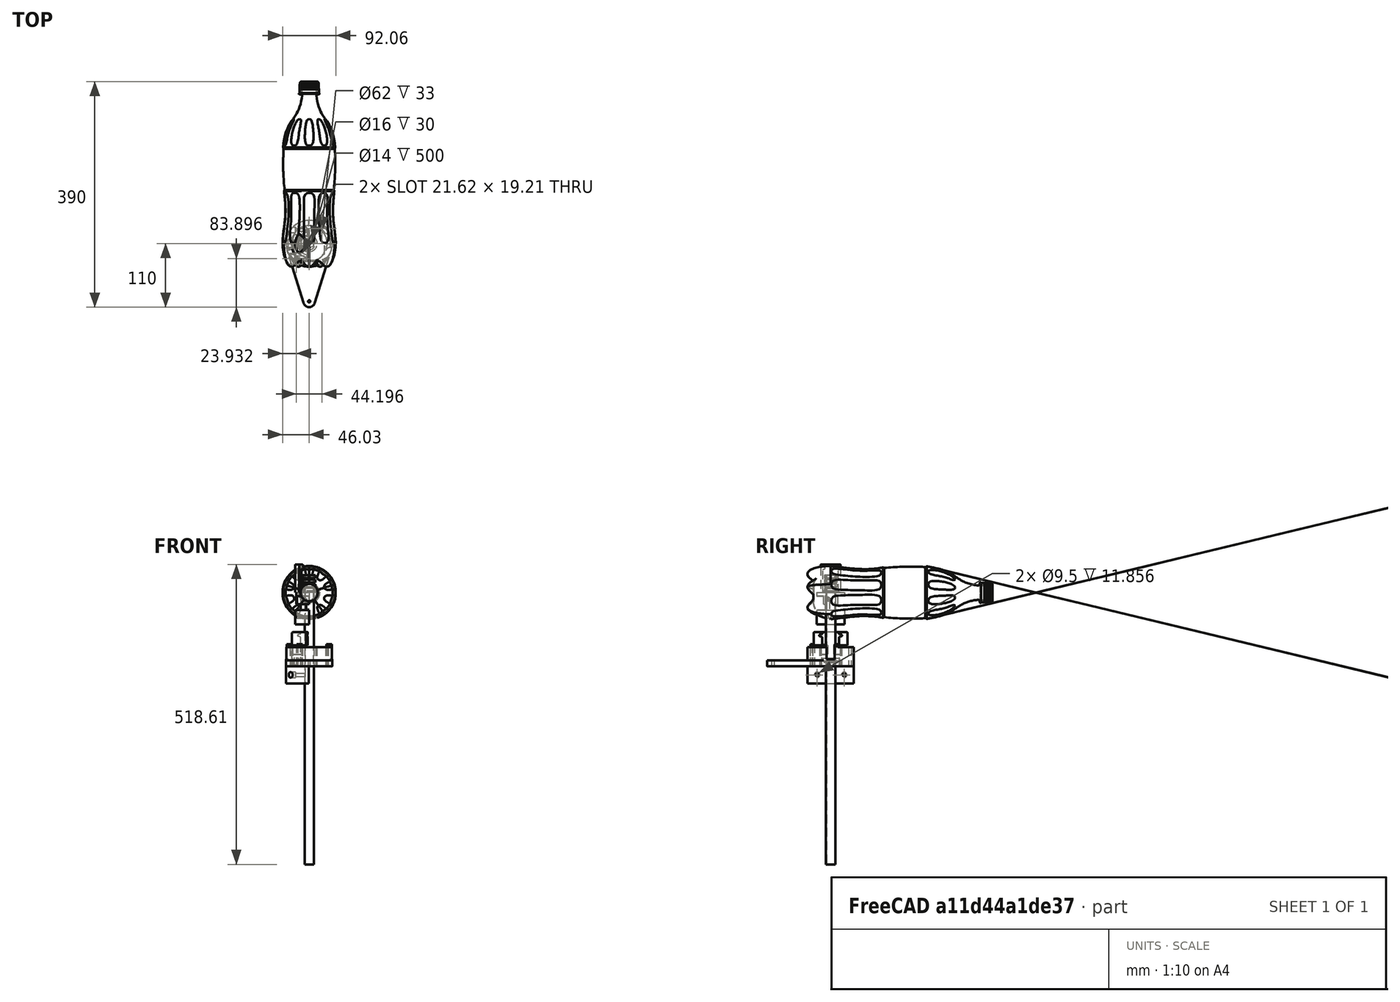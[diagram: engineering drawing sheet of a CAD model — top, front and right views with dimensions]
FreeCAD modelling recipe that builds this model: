
FCSTD DOCUMENT  (FreeCAD 0.17R10694 (Git))
Label: launchBase
License: All rights reserved
LicenseURL: http://en.wikipedia.org/wiki/All_rights_reserved
objects: Sketcher::SketchObject×26, PartDesign::Pocket×13, PartDesign::Plane×12, PartDesign::Pad×10, PartDesign::Body×7, App::Part×5, PartDesign::Line×5, PartDesign::Revolution×3, Mesh::Feature×3, Part::Feature×2, PartDesign::ShapeBinder×2, PartDesign::Fillet×2, PartDesign::AdditiveCylinder×1, PartDesign::SubtractiveCylinder×1, PartDesign::LinearPattern×1, PartDesign::Mirrored×1, PartDesign::Chamfer×1, PartDesign::PolarPattern×1
note: 116 computed .brp shape members not serialized (recipe doc carries the construction recipe); baked Part::Feature solids carry a one-line shape summary decoded from their .brp

FEATURE [Sketcher::SketchObject] Sketch
  MapMode = 5
  Placement = pos=(0,0,0) rot=(1,0,0;1.5708rad)
  Support = -> [XZ_Plane001]
  sketch-geometry (18):
    g0: LineSegment StartX=8 StartY=0 StartZ=0 EndX=8 EndY=30 EndZ=0
    g1: LineSegment StartX=8 StartY=30 StartZ=0 EndX=10.6 EndY=30 EndZ=0
    g2: LineSegment StartX=10.6 StartY=30 StartZ=0 EndX=10.6 EndY=25 EndZ=0
    g3: LineSegment StartX=10.6 StartY=25 StartZ=0 EndX=8.5 EndY=25 EndZ=0
    g4: LineSegment StartX=8.5 StartY=25 StartZ=0 EndX=8.5 EndY=22.5 EndZ=0
    g5: LineSegment StartX=8.5 StartY=22.5 StartZ=0 EndX=10.6 EndY=22.5 EndZ=0
    g6: LineSegment StartX=10.6 StartY=22.5 StartZ=0 EndX=10.6 EndY=17.5 EndZ=0
    g7: LineSegment StartX=10.6 StartY=17.5 StartZ=0 EndX=8.5 EndY=17.5 EndZ=0
    g8: LineSegment StartX=8.5 StartY=17.5 StartZ=0 EndX=8.5 EndY=15 EndZ=0
    g9: LineSegment StartX=8.5 StartY=15 StartZ=0 EndX=10.6 EndY=15 EndZ=0
    g10: LineSegment StartX=10.6 StartY=15 StartZ=0 EndX=10.6 EndY=10 EndZ=0
    g11: LineSegment StartX=10.6 StartY=10 StartZ=0 EndX=8.5 EndY=10 EndZ=0
    g12: LineSegment StartX=8.5 StartY=10 StartZ=0 EndX=8.5 EndY=7.5 EndZ=0
    g13: LineSegment StartX=8.5 StartY=7.5 StartZ=0 EndX=10.6 EndY=7.5 EndZ=0
    g14: LineSegment StartX=14 StartY=0 StartZ=0 EndX=8 EndY=0 EndZ=0
    g15: LineSegment StartX=10.6 StartY=7.5 StartZ=0 EndX=10.6 EndY=3 EndZ=0
    g16: LineSegment StartX=10.6 StartY=3 StartZ=0 EndX=14 EndY=3 EndZ=0
    g17: LineSegment StartX=14 StartY=3 StartZ=0 EndX=14 EndY=0 EndZ=0
  constraints (55):
    c: PointOnObject(g0,g-1)
    c: Vertical(g0)
    c: Coincident(g0,g1)
    c: Horizontal(g1)
    c: Coincident(g1,g2)
    c: Vertical(g2)
    c: Coincident(g2,g3)
    c: Coincident(g3,g4)
    c: Coincident(g4,g5)
    c: Coincident(g5,g6)
    c: Coincident(g6,g7)
    c: Coincident(g7,g8)
    c: Coincident(g8,g9)
    c: Horizontal(g9)
    c: Coincident(g9,g10)
    c: Coincident(g10,g11)
    c: Horizontal(g11)
    c: Coincident(g11,g12)
    c: Coincident(g12,g13)
    c: Coincident(g14,g0)
    c: Horizontal(g14)
    c: DistanceY(g0,g0) = 30
    c: DistanceX(g-1,g0) = 8
    c: Horizontal(g3)
    c: Horizontal(g7)
    c: Horizontal(g13)
    c: DistanceY(g2,g2) = 5
    c: Vertical(g12)
    c: Vertical(g10)
    c: Vertical(g8)
    c: Vertical(g4)
    c: Horizontal(g5)
    c: Equal(g4,g8)
    c: Equal(g8,g12)
    c: DistanceY(g4,g4) = 2.5
    c: Vertical(g6)
    c: Equal(g3,g5)
    c: Equal(g5,g7)
    c: Equal(g7,g9)
    c: Equal(g9,g11)
    c: Equal(g11,g13)
    c: DistanceX(g12) = 8.5
    c: Equal(g6,g10)
    c: DistanceY(g6,g6) = 5
    c: Coincident(g15,g13)
    c: Vertical(g15)
    c: Coincident(g16,g15)
    c: Horizontal(g16)
    c: Coincident(g17,g16)
    c: PointOnObject(g17,g-1)
    c: Vertical(g17)
    c: DistanceX(g1) = 10.6
    c: Coincident(g14,g17)
    c: DistanceX(g14,g14) = 6
    c: DistanceY(g17,g17) = 3
FEATURE [PartDesign::Revolution] Revolution
  Angle = 360
  Axis = (0,0,1)
  Base = (0,0,0)
  Placement = pos=(0,0,0) rot=(1,0,0;1.5708rad)
  Profile = -> Sketch
  ReferenceAxis = -> Sketch [V_Axis]
  Reversed = true
FEATURE [PartDesign::Body] Body
  Group = -> [Sketch,Revolution]
  Origin = -> BodyOrigin
  Tip = -> Revolution
FEATURE [App::Part] Part  label="nozzleHolder"
  Group = -> [Body]
  License = CC BY 3.0
  LicenseURL = http://creativecommons.org/licenses/by/3.0/
  Origin = -> PartOrigin
  Placement = pos=(0,0,-94) rot=(0,0,1;0rad)
FEATURE [PartDesign::AdditiveCylinder] Cylinder
  Angle = 360
  AttacherType = Attacher::AttachEngine3D
  Height = 500
  MapMode = 45
  Placement = pos=(0,0,30) rot=(0,1,0;3.14159rad)
  Radius = 8
  Support = -> [Revolution]
FEATURE [PartDesign::SubtractiveCylinder] Cylinder001
  Angle = 360
  AttacherType = Attacher::AttachEngine3D
  BaseFeature = -> Cylinder
  Height = 1500
  MapMode = 5
  Placement = pos=(0,0,30) rot=(1,0,0;3.14159rad)
  Radius = 7
  Support = -> [Cylinder]
FEATURE [PartDesign::Body] Body001
  Group = -> [Cylinder,Cylinder001]
  Origin = -> Body001Origin
  Tip = -> Cylinder001
FEATURE [App::Part] Part001  label="centralTube"
  Group = -> [Body001]
  License = CC BY 3.0
  LicenseURL = http://creativecommons.org/licenses/by/3.0/
  Origin = -> Part001Origin
  Placement = pos=(0,0,150) rot=(0,0,1;0rad)
FEATURE [Part::Feature] Part__Feature  label="bottle004"
  shape: bbox 37.16 x 19.53 x 37.16 mm, 289 faces (baked)
FEATURE [Part::Feature] Part__Feature001  label="bottle005"
  shape: bbox 103.6 x 317 x 103.7 mm, 79 faces (baked)
FEATURE [App::Part] bottle3  label="bottle006"
  Group = -> [Part__Feature,Part__Feature001]
  License = CC BY 3.0
  LicenseURL = http://creativecommons.org/licenses/by/3.0/
  Origin = -> bottle3Origin
  Placement = pos=(0,0,185) rot=(-1,0,0;1.5708rad)
FEATURE [Sketcher::SketchObject] Sketch001
  MapMode = 5
  Placement = pos=(0,0,0) rot=(1,0,0;1.5708rad)
  Support = -> [XZ_Plane006]
  sketch-geometry (10):
    g0: LineSegment StartX=-13.8661 StartY=42.1125 StartZ=0 EndX=-15.7025 EndY=47.8456 EndZ=0
    g1: LineSegment StartX=-16.75 StartY=48.61 StartZ=0 EndX=-23.14 EndY=48.61 EndZ=0
    g2: LineSegment StartX=-24.16 StartY=47.59 StartZ=0 EndX=-24.16 EndY=0 EndZ=0
    g3: LineSegment StartX=-24.16 StartY=0 StartZ=0 EndX=-19.16 EndY=0 EndZ=0
    g4: LineSegment StartX=-19.16 StartY=0 StartZ=0 EndX=-19.16 EndY=39.34 EndZ=0
    g5: LineSegment StartX=-18.5754 StartY=40.0874 StartZ=0 EndX=-14.4212 EndY=41.1175 EndZ=0
    g6: ArcOfCircle CenterX=-14.6089 CenterY=41.8745 CenterZ=0 NormalX=0 NormalY=0 NormalZ=1 Radius=0.78 StartAngle=4.95545 EndAngle=6.59317
    g7: ArcOfCircle CenterX=-16.75 CenterY=47.51 CenterZ=0 NormalX=0 NormalY=0 NormalZ=1 Radius=1.1 StartAngle=0.309988 EndAngle=1.5708
    g8: ArcOfCircle CenterX=-23.14 CenterY=47.59 CenterZ=0 NormalX=0 NormalY=0 NormalZ=1 Radius=1.02 StartAngle=1.5708 EndAngle=3.14159
    g9: ArcOfCircle CenterX=-18.39 CenterY=39.34 CenterZ=0 NormalX=0 NormalY=0 NormalZ=1 Radius=0.77 StartAngle=1.81386 EndAngle=3.14159
  constraints (26):
    c: Horizontal(g1)
    c: Vertical(g2)
    c: Coincident(g2,g3)
    c: Horizontal(g3)
    c: Coincident(g3,g4)
    c: Vertical(g4)
    c: Tangent(g0,g6) = -1.5708
    c: Tangent(g5,g6) = -1.5708
    c: Tangent(g0,g7) = -1.5708
    c: Tangent(g1,g7) = -1.5708
    c: Tangent(g1,g8) = -1.5708
    c: Tangent(g2,g8) = -1.5708
    c: Tangent(g4,g9) = 1.5708
    c: Tangent(g5,g9) = 1.5708
    c: DistanceX(g3) = -19.16
    c: DistanceY(g3) = 0
    c: DistanceX(g3,g3) = 5
    c: DistanceY(g2,g2) = 47.59
    c: Radius(g8) = 1.02
    c: DistanceX(g1,g1) = 6.39
    c: Radius(g7) = 1.1
    c: Distance(g0) = 6.02
    c: Radius(g6) = 0.78
    c: Distance(g5) = 4.28
    c: Radius(g9) = 0.77
    c: DistanceY(g4,g4) = 39.34
FEATURE [PartDesign::Revolution] Revolution001
  Angle = 90
  Axis = (0,0,1)
  Base = (0,0,0)
  Midplane = true
  Placement = pos=(0,0,0) rot=(1,0,0;1.5708rad)
  Profile = -> Sketch001
  ReferenceAxis = -> Sketch001 [V_Axis]
FEATURE [Sketcher::SketchObject] Sketch002
  ExternalGeometry = -> [Revolution001]
  MapMode = 5
  Placement = pos=(0,0,0) rot=(1,0,0;3.14159rad)
  Support = -> [Revolution001]
  sketch-geometry (4):
    g0: ArcOfCircle CenterX=0 CenterY=0 CenterZ=0 NormalX=0 NormalY=0 NormalZ=1 Radius=24.16 StartAngle=1.5708 EndAngle=4.71239
    g1: ArcOfCircle CenterX=0 CenterY=0 CenterZ=0 NormalX=0 NormalY=0 NormalZ=1 Radius=9 StartAngle=1.5708 EndAngle=4.71239
    g2: LineSegment StartX=0 StartY=24.16 StartZ=0 EndX=0 EndY=9 EndZ=0
    g3: LineSegment StartX=0 StartY=-9 StartZ=0 EndX=0 EndY=-24.16 EndZ=0
  constraints (13):
    c: Coincident(g0,g-1)
    c: Coincident(g0,g-3)
    c: Coincident(g0,g-3)
    c: Coincident(g1,g-1)
    c: PointOnObject(g1,g-2)
    c: PointOnObject(g1,g-2)
    c: Coincident(g2,g0)
    c: Vertical(g2)
    c: Coincident(g3,g1)
    c: Vertical(g3)
    c: Radius(g1) = 9
    c: Coincident(g0,g3)
    c: Coincident(g2,g1)
FEATURE [PartDesign::Pad] Pad
  BaseFeature = -> Revolution001
  Length = 20
  Length2 = 100
  Placement = pos=(0,0,0) rot=(1,0,0;1.5708rad)
  Profile = -> Sketch002
  Type = 0
FEATURE [Sketcher::SketchObject] Sketch003
  ExternalGeometry = -> [Pad]
  MapMode = 5
  Placement = pos=(0,0,0) rot=(0.707107,0,0.707107;3.14159rad)
  Support = -> [Pad]
  sketch-geometry (8):
    g0: LineSegment StartX=-20 StartY=24.16 StartZ=0 EndX=-6 EndY=24.16 EndZ=0
    g1: LineSegment StartX=-6 StartY=24.16 StartZ=0 EndX=-6 EndY=12 EndZ=0
    g2: LineSegment StartX=-6 StartY=12 StartZ=0 EndX=-20 EndY=12 EndZ=0
    g3: LineSegment StartX=-20 StartY=12 StartZ=0 EndX=-20 EndY=24.16 EndZ=0
    g4: LineSegment StartX=-20 StartY=-24.16 StartZ=0 EndX=-6 EndY=-24.16 EndZ=0
    g5: LineSegment StartX=-6 StartY=-24.16 StartZ=0 EndX=-6 EndY=-12 EndZ=0
    g6: LineSegment StartX=-6 StartY=-12 StartZ=0 EndX=-20 EndY=-12 EndZ=0
    g7: LineSegment StartX=-20 StartY=-12 StartZ=0 EndX=-20 EndY=-24.16 EndZ=0
  constraints (18):
    c: Coincident(g0,g1)
    c: Coincident(g1,g2)
    c: Coincident(g2,g3)
    c: Coincident(g3,g0)
    c: Horizontal(g0)
    c: Horizontal(g2)
    c: Vertical(g1)
    c: Vertical(g3)
    c: Coincident(g4,g5)
    c: Coincident(g5,g6)
    c: Coincident(g6,g7)
    c: Coincident(g7,g4)
    c: Horizontal(g4)
    c: Horizontal(g6)
    c: Vertical(g5)
    c: Vertical(g7)
    c: Equal(g6,g2)
    c: Equal(g1,g5)
FEATURE [PartDesign::Pocket] Pocket
  BaseFeature = -> Pad
  Length = 5
  Placement = pos=(0,0,0) rot=(1,0,0;1.5708rad)
  Profile = -> Sketch003
  Type = 1
FEATURE [Sketcher::SketchObject] Sketch004
  ExternalGeometry = -> [Pocket]
  MapMode = 5
  Placement = pos=(0,0,-6) rot=(1,0,0;3.14159rad)
  Support = -> [Pocket]
  sketch-geometry (1):
    g0: Circle CenterX=-10 CenterY=-5 CenterZ=0 NormalX=0 NormalY=0 NormalZ=1 Radius=2
  constraints (3):
    c: Radius(g0) = 2
    c: DistanceY(g-3,g0) = 7
    c: DistanceX(g0,g-3) = 10
FEATURE [PartDesign::Pocket] Pocket001
  BaseFeature = -> Pocket
  Length = 5
  Placement = pos=(0,0,0) rot=(1,0,0;1.5708rad)
  Profile = -> Sketch004
  Type = 1
FEATURE [PartDesign::Line] DatumLine
  AttacherType = Attacher::AttachEngineLine
  MapMode = 19
  Placement = pos=(-10,0,-13) rot=(1,0,0;1.5708rad)
FEATURE [Sketcher::SketchObject] Sketch007
  ExternalGeometry = -> [Pocket001]
  MapMode = 5
  Placement = pos=(0,0,-20) rot=(1,0,0;3.14159rad)
  Support = -> [Pocket001]
  sketch-geometry (4):
    g0: LineSegment StartX=-25 StartY=-9 StartZ=0 EndX=0 EndY=-9 EndZ=0
    g1: LineSegment StartX=0 StartY=-9 StartZ=0 EndX=0 EndY=9 EndZ=0
    g2: LineSegment StartX=0 StartY=9 StartZ=0 EndX=-25 EndY=9 EndZ=0
    g3: LineSegment StartX=-25 StartY=9 StartZ=0 EndX=-25 EndY=-9 EndZ=0
  constraints (11):
    c: Coincident(g0,g1)
    c: Coincident(g1,g2)
    c: Coincident(g2,g3)
    c: Coincident(g3,g0)
    c: Horizontal(g0)
    c: Horizontal(g2)
    c: Vertical(g1)
    c: Vertical(g3)
    c: Symmetric(g0,g1,g-1)
    c: Coincident(g0,g-3)
    c: DistanceX(g0,g0) = 25
FEATURE [PartDesign::Pocket] Pocket002
  BaseFeature = -> Pocket001
  Length = 20
  Placement = pos=(0,0,0) rot=(1,0,0;1.5708rad)
  Profile = -> Sketch007
  Type = 0
FEATURE [PartDesign::Body] Body002  label="clamp"
  Group = -> [Sketch001,Revolution001,Sketch002,Pad,Sketch003,Pocket,Sketch004,Pocket001,Sketch007,Pocket002]
  Origin = -> Body002Origin
  Tip = -> Pocket002
FEATURE [PartDesign::ShapeBinder] ReferencePocket002
  Placement = pos=(0,0,0) rot=(1,0,0;1.5708rad)
  Support = -> [Pocket002]
FEATURE [PartDesign::Plane] DatumPlane
  MapMode = 5
  Placement = pos=(0,-9,0) rot=(-1,0,0;1.5708rad)
  Support = -> [ReferencePocket002]
FEATURE [Sketcher::SketchObject] Sketch008
  ExternalGeometry = -> [ReferencePocket002]
  MapMode = 5
  Placement = pos=(0,-9,0) rot=(-1,0,0;1.5708rad)
  Support = -> [DatumPlane]
  sketch-geometry (6):
    g0: Circle CenterX=-10 CenterY=13 CenterZ=0 NormalX=0 NormalY=0 NormalZ=1 Radius=2
    g1: ArcOfCircle CenterX=-10 CenterY=13 CenterZ=0 NormalX=0 NormalY=0 NormalZ=1 Radius=5 StartAngle=3.14159 EndAngle=6.28319
    g2: LineSegment [constr] StartX=-15 StartY=13 StartZ=0 EndX=-5 EndY=13 EndZ=0
    g3: LineSegment StartX=-15 StartY=13 StartZ=0 EndX=-15 EndY=30 EndZ=0
    g4: LineSegment StartX=-15 StartY=30 StartZ=0 EndX=-5 EndY=30 EndZ=0
    g5: LineSegment StartX=-5 StartY=30 StartZ=0 EndX=-5 EndY=13 EndZ=0
  constraints (16):
    c: Coincident(g0,g-3)
    c: Equal(g0,g-3)
    c: Coincident(g1,g0)
    c: Coincident(g2,g1)
    c: Horizontal(g2)
    c: PointOnObject(g0,g2)
    c: Coincident(g1,g2)
    c: Vertical(g3)
    c: Coincident(g3,g4)
    c: Horizontal(g4)
    c: Coincident(g4,g5)
    c: Coincident(g5,g1)
    c: Vertical(g5)
    c: DistanceX(g4,g4) = 10
    c: DistanceY(g5,g5) = 17
    c: Coincident(g1,g3)
FEATURE [PartDesign::Pad] Pad001
  Length = 11
  Length2 = 100
  Placement = pos=(0,-9,0) rot=(-1,0,0;1.5708rad)
  Profile = -> Sketch008
  Type = 0
FEATURE [PartDesign::Plane] DatumPlane001
  MapMode = 5
  Placement = pos=(0,-9,-30) rot=(0,1,0;3.14159rad)
  Support = -> [Pad001]
FEATURE [PartDesign::ShapeBinder] ReferenceRevolution
  Placement = pos=(0,0,0) rot=(1,0,0;1.5708rad)
  Support = -> [Revolution]
FEATURE [PartDesign::Line] DatumLine001
  AttacherType = Attacher::AttachEngineLine
  MapMode = 42
  Support = -> [ReferenceRevolution]
FEATURE [Sketcher::SketchObject] Sketch009
  ExternalGeometry = -> [DatumLine001]
  MapMode = 5
  Placement = pos=(0,-9,-30) rot=(0,1,0;3.14159rad)
  Support = -> [DatumPlane001]
  sketch-geometry (4):
    g0: ArcOfCircle CenterX=0 CenterY=9 CenterZ=0 NormalX=0 NormalY=0 NormalZ=1 Radius=24 StartAngle=4.71239 EndAngle=7.85398
    g1: LineSegment StartX=0 StartY=33 StartZ=0 EndX=0 EndY=17 EndZ=0
    g2: ArcOfCircle CenterX=0 CenterY=9 CenterZ=0 NormalX=0 NormalY=0 NormalZ=1 Radius=8 StartAngle=4.71239 EndAngle=7.85398
    g3: LineSegment StartX=0 StartY=1 StartZ=0 EndX=0 EndY=-15 EndZ=0
  constraints (13):
    c: Coincident(g0,g-3)
    c: PointOnObject(g0,g-2)
    c: PointOnObject(g1,g-2)
    c: Vertical(g1)
    c: Coincident(g2,g0)
    c: Coincident(g2,g1)
    c: PointOnObject(g2,g-2)
    c: Coincident(g3,g2)
    c: Coincident(g3,g0)
    c: Vertical(g3)
    c: Radius(g2) = 8
    c: Radius(g0) = 24
    c: Coincident(g1,g0)
FEATURE [PartDesign::Pad] Pad002
  BaseFeature = -> Pad001
  Length = 25
  Length2 = 100
  Placement = pos=(0,-9,0) rot=(-1,0,0;1.5708rad)
  Profile = -> Sketch009
  Type = 0
FEATURE [PartDesign::LinearPattern] LinearPattern
  BaseFeature = -> Pad002
  Direction = -> Sketch008 [N_Axis]
  Length = 35
  Occurrences = 2
  Originals = -> [Pad001]
  Placement = pos=(0,-9,0) rot=(-1,0,0;1.5708rad)
  Reversed = true
FEATURE [Sketcher::SketchObject] Sketch010
  ExternalGeometry = -> [LinearPattern]
  MapMode = 5
  Placement = pos=(0,-9,0) rot=(0,1,0;1.5708rad)
  Support = -> [LinearPattern]
  sketch-geometry (4):
    g0: LineSegment [constr] StartX=30 StartY=12 StartZ=0 EndX=55 EndY=-4 EndZ=0
    g1: LineSegment [constr] StartX=30 StartY=-36 StartZ=0 EndX=55 EndY=-20 EndZ=0
    g2: Circle CenterX=42.5 CenterY=4 CenterZ=0 NormalX=0 NormalY=0 NormalZ=1 Radius=2
    g3: Circle CenterX=42.5 CenterY=-28 CenterZ=0 NormalX=0 NormalY=0 NormalZ=1 Radius=2
  constraints (6):
    c: PointOnObject(g2,g0)
    c: PointOnObject(g3,g1)
    c: Equal(g2,g3)
    c: Symmetric(g0,g0,g2)
    c: Symmetric(g1,g1,g3)
    c: Radius(g3) = 2
FEATURE [PartDesign::Pocket] Pocket003
  BaseFeature = -> LinearPattern
  Length = 5
  Placement = pos=(0,-9,0) rot=(-1,0,0;1.5708rad)
  Profile = -> Sketch010
  Type = 1
FEATURE [Sketcher::SketchObject] Sketch012
  ExternalGeometry = -> [Pocket003]
  MapMode = 5
  Placement = pos=(0,-9,-30) rot=(0,1,0;3.14159rad)
  Support = -> [DatumPlane001]
  sketch-geometry (4):
    g0: ArcOfCircle CenterX=0 CenterY=-12 CenterZ=0 NormalX=0 NormalY=0 NormalZ=1 Radius=31.88 StartAngle=4.71239 EndAngle=7.85398
    g1: ArcOfCircle CenterX=0 CenterY=-12 CenterZ=0 NormalX=0 NormalY=0 NormalZ=1 Radius=20 StartAngle=4.71239 EndAngle=7.85398
    g2: LineSegment StartX=0 StartY=19.88 StartZ=0 EndX=0 EndY=8 EndZ=0
    g3: LineSegment StartX=0 StartY=-32 StartZ=0 EndX=0 EndY=-43.88 EndZ=0
  constraints (15):
    c: PointOnObject(g0,g-2)
    c: PointOnObject(g0,g-2)
    c: PointOnObject(g1,g-2)
    c: PointOnObject(g1,g-2)
    c: PointOnObject(g1,g-2)
    c: Coincident(g0,g1)
    c: Coincident(g0,g-3)
    c: Radius(g1) = 20
    c: PointOnObject(g2,g-2)
    c: PointOnObject(g2,g-2)
    c: Coincident(g1,g2)
    c: Coincident(g0,g2)
    c: Coincident(g0,g3)
    c: Coincident(g1,g3)
    c: Radius(g0) = 31.88
FEATURE [PartDesign::Pocket] Pocket005
  BaseFeature = -> Pocket003
  Length = 25
  Placement = pos=(0,-9,0) rot=(-1,0,0;1.5708rad)
  Profile = -> Sketch012
  Type = 0
FEATURE [PartDesign::Body] Body003  label="fixation"
  Group = -> [DatumLine,DatumPlane,ReferencePocket002,Sketch008,Pad001,DatumPlane001,DatumLine001,ReferenceRevolution,Sketch009,Pad002,LinearPattern,Sketch010,Pocket003,Sketch012,Pocket005]
  Origin = -> Body003Origin
  Tip = -> Pocket005
FEATURE [App::Part] Part002  label="releasmechanism"
  Group = -> [Body002,Body003]
  License = CC BY 3.0
  LicenseURL = http://creativecommons.org/licenses/by/3.0/
  Origin = -> Part002Origin
  Placement = pos=(0,0,-113) rot=(0,0,1;0rad)
FEATURE [Sketcher::SketchObject] Sketch013
  MapMode = 5
  Placement = pos=(0,0,0) rot=(1,0,0;1.5708rad)
  Support = -> [XZ_Plane009]
  sketch-geometry (14):
    g0: LineSegment StartX=-14.5926 StartY=-91.2916 StartZ=0 EndX=-14.5926 EndY=-78.1016 EndZ=0
    g1: LineSegment StartX=-15.6271 StartY=-76.6684 StartZ=0 EndX=-19.0629 EndY=-75.5285 EndZ=0
    g2: LineSegment StartX=-19.8645 StartY=-74.4181 StartZ=0 EndX=-19.8645 EndY=-73.7281 EndZ=0
    g3: LineSegment StartX=-19.1362 StartY=-72.7285 StartZ=0 EndX=-15.1 EndY=-71.4297 EndZ=0
    g4: LineSegment StartX=-14.4411 StartY=-70.3425 StartZ=0 EndX=-14.6117 EndY=-69.347 EndZ=0
    g5: LineSegment StartX=-15.9226 StartY=-68.2416 StartZ=0 EndX=-27.9326 EndY=-68.2416 EndZ=0
    g6: LineSegment StartX=-29.6526 StartY=-69.9616 StartZ=0 EndX=-29.6526 EndY=-91.2916 EndZ=0
    g7: LineSegment StartX=-29.6526 StartY=-91.2916 StartZ=0 EndX=-14.5926 EndY=-91.2916 EndZ=0
    g8: ArcOfCircle CenterX=-16.1026 CenterY=-78.1016 CenterZ=0 NormalX=0 NormalY=0 NormalZ=1 Radius=1.51 StartAngle=0 EndAngle=1.25046
    g9: ArcOfCircle CenterX=-18.6945 CenterY=-74.4181 CenterZ=0 NormalX=0 NormalY=0 NormalZ=1 Radius=1.17 StartAngle=3.14159 EndAngle=4.39205
    g10: ArcOfCircle CenterX=-18.8145 CenterY=-73.7281 CenterZ=0 NormalX=0 NormalY=0 NormalZ=1 Radius=1.05 StartAngle=1.88214 EndAngle=3.14159
    g11: ArcOfCircle CenterX=-15.3972 CenterY=-70.5063 CenterZ=0 NormalX=0 NormalY=0 NormalZ=1 Radius=0.97 StartAngle=5.02373 EndAngle=6.4529
    g12: ArcOfCircle CenterX=-15.9226 CenterY=-69.5716 CenterZ=0 NormalX=0 NormalY=0 NormalZ=1 Radius=1.33 StartAngle=0.16971 EndAngle=1.5708
    g13: ArcOfCircle CenterX=-27.9326 CenterY=-69.9616 CenterZ=0 NormalX=0 NormalY=0 NormalZ=1 Radius=1.72 StartAngle=1.5708 EndAngle=3.14159
  constraints (36):
    c: Vertical(g2)
    c: Horizontal(g5)
    c: Vertical(g6)
    c: Coincident(g6,g7)
    c: Coincident(g7,g0)
    c: Horizontal(g7)
    c: Vertical(g0)
    c: Tangent(g0,g8) = -1.5708
    c: Tangent(g1,g8) = -1.5708
    c: Tangent(g1,g9) = 1.5708
    c: Tangent(g2,g9) = 1.5708
    c: Tangent(g2,g10) = 1.5708
    c: Tangent(g3,g10) = 1.5708
    c: Tangent(g3,g11) = -1.5708
    c: Tangent(g4,g11) = -1.5708
    c: Tangent(g4,g12) = -1.5708
    c: Tangent(g5,g12) = -1.5708
    c: Tangent(g5,g13) = -1.5708
    c: Tangent(g6,g13) = -1.5708
    c: DistanceY(g6,g6) = 21.33
    c: Radius(g13) = 1.72
    c: DistanceX(g5,g5) = 12.01
    c: Radius(g12) = 1.33
    c: Distance(g4) = 1.01
    c: Radius(g11) = 0.97
    c: Distance(g3) = 4.24
    c: Radius(g10) = 1.05
    c: DistanceY(g2,g2) = 0.69
    c: Radius(g9) = 1.17
    c: Distance(g1) = 3.62
    c: Radius(g8) = 1.51
    c: DistanceY(g0,g0) = 13.19
    c: DistanceX(g7,g7) = 15.06
    c: DistanceX(g0) = -14.5926
    c: DistanceY(g0) = -91.2916
    c: DistanceY(g1,g3) = 2.8
FEATURE [PartDesign::Revolution] Revolution002
  Angle = 160
  Axis = (0,0,1)
  Base = (0,0,0)
  Midplane = true
  Placement = pos=(0,0,0) rot=(1,0,0;1.5708rad)
  Profile = -> Sketch013
  ReferenceAxis = -> Sketch013 [V_Axis]
FEATURE [Sketcher::SketchObject] Sketch014
  ExternalGeometry = -> [Revolution002]
  MapMode = 5
  Placement = pos=(0,0,-91.2916) rot=(1,0,0;3.14159rad)
  Support = -> [Revolution002]
  sketch-geometry (4):
    g0: LineSegment StartX=-29.228 StartY=5 StartZ=0 EndX=-13.7092 EndY=5 EndZ=0
    g1: LineSegment StartX=-29.228 StartY=-5 StartZ=0 EndX=-13.7092 EndY=-5 EndZ=0
    g2: ArcOfCircle CenterX=0 CenterY=0 CenterZ=0 NormalX=0 NormalY=0 NormalZ=1 Radius=29.6526 StartAngle=2.97216 EndAngle=3.31102
    g3: ArcOfCircle CenterX=0 CenterY=0 CenterZ=0 NormalX=0 NormalY=0 NormalZ=1 Radius=14.5926 StartAngle=2.79187 EndAngle=3.49132
  constraints (14):
    c: PointOnObject(g0,g-3)
    c: PointOnObject(g0,g-4)
    c: Horizontal(g0)
    c: PointOnObject(g1,g-3)
    c: PointOnObject(g1,g-4)
    c: Horizontal(g1)
    c: Coincident(g2,g-1)
    c: Coincident(g2,g0)
    c: Coincident(g2,g1)
    c: Coincident(g3,g-1)
    c: Coincident(g3,g0)
    c: Coincident(g3,g1)
    c: Symmetric(g0,g1,g-1)
    c: DistanceY(g1,g0) = 10
FEATURE [PartDesign::Pad] Pad003
  BaseFeature = -> Revolution002
  Length = 35
  Length2 = 100
  Placement = pos=(0,0,0) rot=(1,0,0;1.5708rad)
  Profile = -> Sketch014
  Type = 0
FEATURE [PartDesign::Fillet] Fillet
  Base = -> Pad003 [Edge50]
  BaseFeature = -> Pad003
  Placement = pos=(0,0,0) rot=(1,0,0;1.5708rad)
  Radius = 10
FEATURE [Sketcher::SketchObject] Sketch016
  ExternalGeometry = -> [Fillet]
  MapMode = 5
  Placement = pos=(0,-5,0) rot=(1,0,0;1.5708rad)
  Support = -> [Fillet]
  sketch-geometry (3):
    g0: LineSegment [constr] StartX=-19.0059 StartY=-126.292 StartZ=0 EndX=-19.0059 EndY=-116.292 EndZ=0
    g1: LineSegment [constr] StartX=-29.228 StartY=-116.292 StartZ=0 EndX=-19.0059 EndY=-116.292 EndZ=0
    g2: Circle CenterX=-19.0059 CenterY=-116.292 CenterZ=0 NormalX=0 NormalY=0 NormalZ=1 Radius=2.1
  constraints (7):
    c: Vertical(g0)
    c: Coincident(g1,g0)
    c: Horizontal(g1)
    c: Coincident(g2,g0)
    c: Radius(g2) = 2.1
    c: Coincident(g0,g-3)
    c: Coincident(g1,g-4)
FEATURE [PartDesign::Pocket] Pocket006
  BaseFeature = -> Fillet
  Length = 5
  Placement = pos=(0,0,0) rot=(1,0,0;1.5708rad)
  Profile = -> Sketch016
  Type = 1
FEATURE [PartDesign::Body] Body004  label="Clamp"
  Group = -> [Sketch013,Revolution002,Sketch014,Pad003,Fillet,Sketch016,Pocket006]
  Origin = -> Body004Origin
  Tip = -> Pocket006
FEATURE [PartDesign::Plane] DatumPlane002
  MapMode = 5
  Placement = pos=(0,0,-127.292) rot=(1,0,0;3.14159rad)
  Support = -> [Pocket006]
  superPlacement = pos=(0,0,1) rot=(0,0,1;0rad)
FEATURE [Sketcher::SketchObject] Sketch017
  MapMode = 5
  Placement = pos=(0,0,-127.292) rot=(1,0,0;3.14159rad)
  Support = -> [DatumPlane002]
  sketch-geometry (4):
    g0: ArcOfCircle CenterX=0 CenterY=0 CenterZ=0 NormalX=0 NormalY=0 NormalZ=1 Radius=7 StartAngle=1.71414 EndAngle=4.56904
    g1: LineSegment StartX=-1 StartY=6.9282 StartZ=0 EndX=-1 EndY=39.9875 EndZ=0
    g2: ArcOfCircle CenterX=0 CenterY=0 CenterZ=0 NormalX=0 NormalY=0 NormalZ=1 Radius=40 StartAngle=1.5958 EndAngle=4.68739
    g3: LineSegment StartX=-1 StartY=-6.9282 StartZ=0 EndX=-1 EndY=-39.9875 EndZ=0
  constraints (12):
    c: Coincident(g0,g-1)
    c: DistanceX(g0,g-1) = 1
    c: Coincident(g1,g0)
    c: Vertical(g1)
    c: Coincident(g2,g-1)
    c: Coincident(g2,g1)
    c: Coincident(g3,g0)
    c: Coincident(g3,g2)
    c: Vertical(g3)
    c: Symmetric(g0,g0,g-1)
    c: Radius(g0) = 7
    c: Radius(g2) = 40
FEATURE [PartDesign::Pad] Pad004
  Length = 30
  Length2 = 100
  Placement = pos=(0,0,-127.292) rot=(1,0,0;3.14159rad)
  Profile = -> Sketch017
  Type = 0
FEATURE [PartDesign::Plane] DatumPlane003
  MapMode = 5
  Placement = pos=(0,-5,0) rot=(1,0,0;1.5708rad)
  Support = -> [Pocket006]
FEATURE [PartDesign::Plane] DatumPlane004
  MapMode = 5
  Placement = pos=(0,5,0) rot=(-1,0,0;1.5708rad)
  Support = -> [Pocket006]
FEATURE [PartDesign::Plane] DatumPlane005
  MapMode = 45
  Placement = pos=(-29.5109,0,-103.792) rot=(0.57735,0.57735,0.57735;2.0944rad)
  Support = -> [Pocket006]
FEATURE [Sketcher::SketchObject] Sketch018
  ExternalGeometry = -> [DatumPlane005,DatumPlane004,DatumPlane003,Pad004]
  MapMode = 5
  Placement = pos=(0,0,-127.292) rot=(0,0,1;0rad)
  Support = -> [Pad004]
  sketch-geometry (4):
    g0: ArcOfCircle CenterX=0 CenterY=0 CenterZ=0 NormalX=0 NormalY=0 NormalZ=1 Radius=30.0191 StartAngle=3.32585 EndAngle=3.68416
    g1: LineSegment StartX=-25.7079 StartY=-15.5 StartZ=0 EndX=-13.7079 EndY=-15.5 EndZ=0
    g2: LineSegment StartX=-13.7079 StartY=-15.5 StartZ=0 EndX=-13.7079 EndY=-5.5 EndZ=0
    g3: LineSegment StartX=-13.7079 StartY=-5.5 StartZ=0 EndX=-29.5109 EndY=-5.5 EndZ=0
  constraints (12):
    c: Coincident(g0,g-1)
    c: Coincident(g1,g0)
    c: Horizontal(g1)
    c: Vertical(g2)
    c: Coincident(g3,g2)
    c: Coincident(g3,g0)
    c: Horizontal(g3)
    c: Coincident(g1,g2)
    c: DistanceY(g2,g2) = 10
    c: PointOnObject(g0,g-3)
    c: DistanceY(g2,g-1) = 5.5
    c: DistanceX(g1,g1) = 12
FEATURE [PartDesign::Pad] Pad005
  BaseFeature = -> Pad004
  Length = 20
  Length2 = 100
  Placement = pos=(0,0,-127.292) rot=(1,0,0;3.14159rad)
  Profile = -> Sketch018
  Type = 0
FEATURE [PartDesign::Mirrored] Mirrored
  BaseFeature = -> Pad005
  MirrorPlane = -> Sketch018 [H_Axis]
  Originals = -> [Pad005]
  Placement = pos=(0,0,-127.292) rot=(1,0,0;3.14159rad)
FEATURE [PartDesign::Line] DatumLine002
  AttacherType = Attacher::AttachEngineLine
  MapMode = 19
  Placement = pos=(-19.0059,-5,-116.292) rot=(1,0,0;1.5708rad)
  Support = -> [Pocket006]
FEATURE [Sketcher::SketchObject] Sketch019
  ExternalGeometry = -> [DatumLine002]
  MapMode = 5
  Placement = pos=(0,-15.5,-127.292) rot=(0,0.707107,-0.707107;3.14159rad)
  Support = -> [Mirrored]
  sketch-geometry (1):
    g0: Circle CenterX=19.0059 CenterY=-11 CenterZ=0 NormalX=0 NormalY=0 NormalZ=1 Radius=2.1
  constraints (2):
    c: Coincident(g0,g-3)
    c: Radius(g0) = 2.1
FEATURE [PartDesign::Pocket] Pocket007
  BaseFeature = -> Mirrored
  Length = 5
  Placement = pos=(0,0,-127.292) rot=(1,0,0;3.14159rad)
  Profile = -> Sketch019
  Type = 1
FEATURE [Sketcher::SketchObject] Sketch020
  ExternalGeometry = -> [Pocket007]
  MapMode = 5
  Placement = pos=(-1,0,-127.292) rot=(0.57735,-0.57735,0.57735;4.18879rad)
  Support = -> [Pocket007]
  sketch-geometry (4):
    g0: LineSegment [constr] StartX=-39.9875 StartY=0 StartZ=0 EndX=-6.9282 EndY=30 EndZ=0
    g1: LineSegment [constr] StartX=6.9282 StartY=30 StartZ=0 EndX=39.9875 EndY=0 EndZ=0
    g2: Circle CenterX=-23.4579 CenterY=15 CenterZ=0 NormalX=0 NormalY=0 NormalZ=1 Radius=2.6
    g3: Circle CenterX=23.4579 CenterY=15 CenterZ=0 NormalX=0 NormalY=0 NormalZ=1 Radius=2.6
  constraints (11):
    c: Coincident(g0,g-4)
    c: Coincident(g0,g-3)
    c: Coincident(g1,g-5)
    c: PointOnObject(g1,g-1)
    c: Coincident(g1,g-6)
    c: PointOnObject(g2,g0)
    c: PointOnObject(g3,g1)
    c: Radius(g3) = 2.6
    c: Equal(g3,g2)
    c: Symmetric(g0,g0,g2)
    c: Symmetric(g1,g1,g3)
FEATURE [PartDesign::Pocket] Pocket008
  BaseFeature = -> Pocket007
  Length = 5
  Placement = pos=(0,0,-127.292) rot=(1,0,0;3.14159rad)
  Profile = -> Sketch020
  Type = 1
FEATURE [PartDesign::Plane] DatumPlane006
  MapMode = 45
  Placement = pos=(-33,-23.4579,-142.292) rot=(0.707107,0,0.707107;3.14159rad)
  Support = -> [Pocket008]
  superPlacement = pos=(0,0,-32) rot=(0,0,1;0rad)
FEATURE [PartDesign::Line] DatumLine003
  AttacherType = Attacher::AttachEngineLine
  MapMode = 19
  Placement = pos=(-1,23.4579,-142.292) rot=(0.57735,-0.57735,0.57735;4.18879rad)
  Support = -> [Pocket008]
FEATURE [PartDesign::Line] DatumLine004
  AttacherType = Attacher::AttachEngineLine
  MapMode = 19
  Placement = pos=(-1,-23.4579,-142.292) rot=(0.57735,-0.57735,0.57735;4.18879rad)
  Support = -> [Pocket008]
FEATURE [Sketcher::SketchObject] Sketch021
  ExternalGeometry = -> [DatumLine003,DatumLine004]
  MapMode = 5
  Placement = pos=(-33,-23.4579,-142.292) rot=(0.707107,0,0.707107;3.14159rad)
  Support = -> [DatumPlane006]
  sketch-geometry (2):
    g0: Circle CenterX=0 CenterY=-46.9157 CenterZ=0 NormalX=0 NormalY=0 NormalZ=1 Radius=4.75
    g1: Circle CenterX=0 CenterY=0 CenterZ=0 NormalX=0 NormalY=0 NormalZ=1 Radius=4.75
  constraints (4):
    c: Radius(g0) = 4.75
    c: Equal(g0,g1)
    c: Coincident(g0,g-3)
    c: Coincident(g1,g-4)
FEATURE [PartDesign::Pocket] Pocket009
  BaseFeature = -> Pocket008
  Length = 19
  Midplane = true
  Placement = pos=(0,0,-127.292) rot=(1,0,0;3.14159rad)
  Profile = -> Sketch021
  Reversed = true
  Type = 0
FEATURE [PartDesign::Plane] DatumPlane007
  MapMode = 5
  Placement = pos=(0,0,-127.292) rot=(0,0,1;0rad)
  Support = -> [Pocket009]
FEATURE [Sketcher::SketchObject] Sketch022
  ExternalGeometry = -> [Pocket009]
  MapMode = 5
  Placement = pos=(0,0,-127.292) rot=(0,0,1;0rad)
  Support = -> [DatumPlane007]
  sketch-geometry (2):
    g0: Circle CenterX=0 CenterY=0 CenterZ=0 NormalX=0 NormalY=0 NormalZ=1 Radius=40
    g1: Circle CenterX=0 CenterY=0 CenterZ=0 NormalX=0 NormalY=0 NormalZ=1 Radius=31
  constraints (4):
    c: Coincident(g0,g-1)
    c: PointOnObject(g-3,g0)
    c: Coincident(g1,g-1)
    c: Radius(g1) = 31
FEATURE [PartDesign::Pad] Pad006
  Length = 33
  Length2 = 100
  Placement = pos=(0,0,-127.292) rot=(0,0,1;0rad)
  Profile = -> Sketch022
  Type = 0
FEATURE [PartDesign::Plane] DatumPlane008
  MapMode = 5
  Placement = pos=(0,-5,0) rot=(1,0,0;1.5708rad)
  Support = -> [Pocket006]
FEATURE [PartDesign::Plane] DatumPlane009
  MapMode = 5
  Placement = pos=(0,5,0) rot=(-1,0,0;1.5708rad)
  Support = -> [Pocket006]
FEATURE [Sketcher::SketchObject] Sketch023
  ExternalGeometry = -> [DatumPlane008,DatumPlane009]
  MapMode = 5
  Placement = pos=(0,0,-94.2916) rot=(0,0,1;0rad)
  Support = -> [Pad006]
  sketch-geometry (4):
    g0: LineSegment StartX=-45 StartY=7 StartZ=0 EndX=45 EndY=7 EndZ=0
    g1: LineSegment StartX=45 StartY=7 StartZ=0 EndX=45 EndY=-7 EndZ=0
    g2: LineSegment StartX=45 StartY=-7 StartZ=0 EndX=-45 EndY=-7 EndZ=0
    g3: LineSegment StartX=-45 StartY=-7 StartZ=0 EndX=-45 EndY=7 EndZ=0
  constraints (12):
    c: Coincident(g0,g1)
    c: Coincident(g1,g2)
    c: Coincident(g2,g3)
    c: Coincident(g3,g0)
    c: Horizontal(g0)
    c: Horizontal(g2)
    c: Vertical(g1)
    c: Vertical(g3)
    c: Symmetric(g2,g0,g-1)
    c: DistanceY(g-1,g0) = 7
    c: DistanceX(g0,g0) = 90
    c: Symmetric(g0,g0,g-2)
FEATURE [PartDesign::Pocket] Pocket010
  BaseFeature = -> Pad006
  Length = 21
  Placement = pos=(0,0,-127.292) rot=(0,0,1;0rad)
  Profile = -> Sketch023
  Type = 0
FEATURE [PartDesign::Chamfer] Chamfer
  Base = -> Pocket010 [Edge23,Edge14]
  BaseFeature = -> Pocket010
  Placement = pos=(0,0,-127.292) rot=(0,0,1;0rad)
  Size = 6
FEATURE [Sketcher::SketchObject] Sketch024
  ExternalGeometry = -> [Chamfer]
  MapMode = 5
  Placement = pos=(0,0,-94.2916) rot=(0,0,1;0rad)
  Support = -> [Chamfer]
  sketch-geometry (6):
    g0: ArcOfCircle CenterX=0 CenterY=0 CenterZ=0 NormalX=0 NormalY=0 NormalZ=1 Radius=38 StartAngle=3.66519 EndAngle=4.36332
    g1: ArcOfCircle CenterX=0 CenterY=0 CenterZ=0 NormalX=0 NormalY=0 NormalZ=1 Radius=33 StartAngle=3.66519 EndAngle=4.36332
    g2: LineSegment StartX=-32.909 StartY=-19 StartZ=0 EndX=-28.5788 EndY=-16.5 EndZ=0
    g3: LineSegment StartX=-12.9968 StartY=-35.7083 StartZ=0 EndX=-11.2867 EndY=-31.0099 EndZ=0
    g4: LineSegment [constr] StartX=0 StartY=0 StartZ=0 EndX=-32.909 EndY=-19 EndZ=0
    g5: LineSegment [constr] StartX=0 StartY=0 StartZ=0 EndX=-12.9968 EndY=-35.7083 EndZ=0
  constraints (16):
    c: Coincident(g0,g-1)
    c: Coincident(g1,g-1)
    c: Coincident(g2,g0)
    c: Coincident(g2,g1)
    c: Coincident(g3,g0)
    c: Coincident(g4,g-1)
    c: Coincident(g4,g0)
    c: Coincident(g5,g-1)
    c: Coincident(g5,g0)
    c: PointOnObject(g3,g5)
    c: Coincident(g1,g3)
    c: PointOnObject(g1,g4)
    c: Angle(g-2,g5) = 2.79253
    c: Angle(g-2,g4) = 2.0944
    c: Distance(g3) = 5
    c: Radius(g0) = 38
FEATURE [PartDesign::Pocket] Pocket011
  BaseFeature = -> Chamfer
  Length = 5
  Placement = pos=(0,0,-127.292) rot=(0,0,1;0rad)
  Profile = -> Sketch024
  Type = 1
FEATURE [PartDesign::PolarPattern] PolarPattern
  Angle = 360
  Axis = -> Sketch024 [N_Axis]
  BaseFeature = -> Pocket011
  Occurrences = 2
  Originals = -> [Pocket011]
  Placement = pos=(0,0,-127.292) rot=(0,0,1;0rad)
FEATURE [PartDesign::Plane] DatumPlane010
  MapMode = 5
  Placement = pos=(0,0,-127.292) rot=(1,0,0;3.14159rad)
  Support = -> [PolarPattern]
FEATURE [Sketcher::SketchObject] Sketch025
  ExternalGeometry = -> [PolarPattern]
  MapMode = 5
  Placement = pos=(0,0,-127.292) rot=(1,0,0;3.14159rad)
  Support = -> [DatumPlane010]
  sketch-geometry (5):
    g0: LineSegment StartX=-12.8258 StartY=35.2385 StartZ=0 EndX=-11.4577 EndY=31.4797 EndZ=0
    g1: ArcOfCircle CenterX=0 CenterY=0 CenterZ=0 NormalX=0 NormalY=0 NormalZ=1 Radius=33.5 StartAngle=1.91986 EndAngle=2.18166
    g2: ArcOfCircle CenterX=0 CenterY=0 CenterZ=0 NormalX=0 NormalY=0 NormalZ=1 Radius=37.5 StartAngle=1.91986 EndAngle=2.18166
    g3: LineSegment StartX=-21.5091 StartY=30.7182 StartZ=0 EndX=-19.2148 EndY=27.4416 EndZ=0
    g4: LineSegment [constr] StartX=0 StartY=0 StartZ=0 EndX=-21.5091 EndY=30.7182 EndZ=0
  constraints (14):
    c: PointOnObject(g0,g-5)
    c: PointOnObject(g0,g-5)
    c: Distance(g0,g0) = 4
    c: Distance(g0,g-5) = 0.5
    c: Coincident(g1,g-1)
    c: Coincident(g1,g0)
    c: Coincident(g2,g-1)
    c: Coincident(g2,g0)
    c: Coincident(g3,g2)
    c: Coincident(g3,g1)
    c: Coincident(g4,g-1)
    c: Coincident(g4,g2)
    c: PointOnObject(g1,g4)
    c: Angle(g-5,g4) = 0.261799
FEATURE [PartDesign::Pad] Pad007
  BaseFeature = -> Pocket009
  Length = 38
  Length2 = 100
  Placement = pos=(0,0,-127.292) rot=(1,0,0;3.14159rad)
  Profile = -> Sketch025
  Reversed = true
  Type = 0
FEATURE [PartDesign::Plane] DatumPlane011
  MapMode = 45
  Placement = pos=(-17.2662,-33.168,-108.292) rot=(-0.945015,0.231244,-0.231244;1.62732rad)
  Support = -> [Pad007]
FEATURE [Sketcher::SketchObject] Sketch026
  MapMode = 5
  Placement = pos=(-17.2662,-33.168,-108.292) rot=(-0.945015,0.231244,-0.231244;1.62732rad)
  Support = -> [DatumPlane011]
  sketch-geometry (1):
    g0: Circle CenterX=0 CenterY=-16.2264 CenterZ=0 NormalX=0 NormalY=0 NormalZ=1 Radius=1.5
  constraints (2):
    c: PointOnObject(g0,g-2)
    c: Radius(g0) = 1.5
FEATURE [PartDesign::Pocket] Pocket012
  BaseFeature = -> Pad007
  Length = 8
  Midplane = true
  Placement = pos=(0,0,-127.292) rot=(1,0,0;3.14159rad)
  Profile = -> Sketch026
  Type = 0
FEATURE [PartDesign::Body] Body005  label="Support"
  Group = -> [DatumPlane002,Sketch017,Pad004,DatumPlane003,DatumPlane004,DatumPlane005,Sketch018,Pad005,Mirrored,DatumLine002,Sketch019,Pocket007,Sketch020,Pocket008,DatumPlane006,DatumLine003,DatumLine004,Sketch021,Pocket009,DatumPlane010,Sketch025,Pad007,DatumPlane011,Sketch026,Pocket012]
  Origin = -> Body005Origin
  Tip = -> Pocket012
FEATURE [PartDesign::Fillet] Fillet001
  Base = -> PolarPattern [Edge34,Edge11]
  BaseFeature = -> PolarPattern
  Placement = pos=(0,0,-127.292) rot=(0,0,1;0rad)
  Radius = 8
FEATURE [Sketcher::SketchObject] Sketch027
  ExternalGeometry = -> [Fillet001]
  MapMode = 5
  Placement = pos=(0,0,-94.2916) rot=(0,0,1;0rad)
  Support = -> [Fillet001]
  sketch-geometry (10):
    g0: LineSegment [constr] StartX=-38.9669 StartY=-9.03226 StartZ=0 EndX=38.9669 EndY=9.03226 EndZ=0
    g1: LineSegment [constr] StartX=-38.0314 StartY=-12.3941 StartZ=0 EndX=38.0314 EndY=12.3941 EndZ=0
    g2: ArcOfCircle CenterX=0 CenterY=0 CenterZ=0 NormalX=0 NormalY=0 NormalZ=1 Radius=31 StartAngle=3.36936 EndAngle=3.45663
    g3: ArcOfCircle CenterX=0 CenterY=0 CenterZ=0 NormalX=0 NormalY=0 NormalZ=1 Radius=40 StartAngle=3.36936 EndAngle=3.45663
    g4: LineSegment StartX=-38.9669 StartY=-9.03226 StartZ=0 EndX=-30.1993 EndY=-7 EndZ=0
    g5: LineSegment StartX=-38.0314 StartY=-12.3941 StartZ=0 EndX=-29.4743 EndY=-9.60541 EndZ=0
    g6: LineSegment StartX=30.1993 StartY=7 StartZ=0 EndX=38.9669 EndY=9.03226 EndZ=0
    g7: LineSegment StartX=38.0314 StartY=12.3941 StartZ=0 EndX=29.4743 EndY=9.60541 EndZ=0
    g8: ArcOfCircle CenterX=0 CenterY=0 CenterZ=0 NormalX=0 NormalY=0 NormalZ=1 Radius=31 StartAngle=0.227771 EndAngle=0.315037
    g9: ArcOfCircle CenterX=0 CenterY=0 CenterZ=0 NormalX=0 NormalY=0 NormalZ=1 Radius=40 StartAngle=0.227771 EndAngle=0.315037
  constraints (28):
    c: PointOnObject(g0,g-3)
    c: PointOnObject(g0,g-6)
    c: PointOnObject(g-4,g0)
    c: PointOnObject(g-1,g0)
    c: PointOnObject(g1,g-3)
    c: PointOnObject(g1,g-6)
    c: PointOnObject(g-1,g1)
    c: Angle(g1,g0) = 3.05433
    c: Coincident(g2,g-1)
    c: PointOnObject(g2,g1)
    c: Coincident(g3,g-1)
    c: Coincident(g4,g3)
    c: Coincident(g4,g2)
    c: Coincident(g5,g3)
    c: Coincident(g5,g2)
    c: Coincident(g3,g1)
    c: PointOnObject(g3,g0)
    c: Coincident(g-4,g2)
    c: Coincident(g6,g-5)
    c: Coincident(g6,g0)
    c: Coincident(g7,g1)
    c: PointOnObject(g7,g1)
    c: Coincident(g8,g-1)
    c: Coincident(g8,g6)
    c: Coincident(g8,g7)
    c: Coincident(g9,g-1)
    c: Coincident(g9,g0)
    c: PointOnObject(g9,g1)
FEATURE [PartDesign::Pad] Pad008
  BaseFeature = -> Fillet001
  Length = 5
  Length2 = 100
  Placement = pos=(0,0,-127.292) rot=(0,0,1;0rad)
  Profile = -> Sketch027
  Type = 0
FEATURE [Sketcher::SketchObject] Sketch028
  ExternalGeometry = -> [Pad008]
  MapMode = 5
  Placement = pos=(0,0,-127.292) rot=(0.975688,0.154973,0.154973;1.59541rad)
  Support = -> [Pad008]
  sketch-geometry (4):
    g0: Circle CenterX=-35.5 CenterY=35.5 CenterZ=0 NormalX=0 NormalY=0 NormalZ=1 Radius=1.5
    g1: LineSegment [constr] StartX=-35.5 StartY=38 StartZ=0 EndX=-35.5 EndY=35.5 EndZ=0
    g2: LineSegment [constr] StartX=35.5 StartY=38 StartZ=0 EndX=35.5 EndY=35.5 EndZ=0
    g3: Circle CenterX=35.5 CenterY=35.5 CenterZ=0 NormalX=0 NormalY=0 NormalZ=1 Radius=1.5
  constraints (12):
    c: Radius(g0) = 1.5
    c: PointOnObject(g1,g-3)
    c: Coincident(g1,g0)
    c: Vertical(g1)
    c: Symmetric(g-3,g-3,g1)
    c: DistanceY(g1,g1) = 2.5
    c: PointOnObject(g2,g-4)
    c: Vertical(g2)
    c: DistanceY(g2,g2) = 2.5
    c: Coincident(g3,g2)
    c: Equal(g3,g0)
    c: Symmetric(g-4,g-4,g2)
FEATURE [PartDesign::Pocket] Pocket013
  BaseFeature = -> Pad008
  Length = 7
  Midplane = true
  Placement = pos=(0,0,-127.292) rot=(0,0,1;0rad)
  Profile = -> Sketch028
  Type = 0
FEATURE [Mesh::Feature] Mesh  label="Clamp (Meshed)"
FEATURE [Mesh::Feature] Mesh001  label="Support (Meshed)"
FEATURE [Sketcher::SketchObject] Sketch029
  ExternalGeometry = -> [Pocket013]
  MapMode = 5
  Placement = pos=(0,0,-127.292) rot=(1,0,0;3.14159rad)
  Support = -> [Pocket013]
  sketch-geometry (5):
    g0: Circle CenterX=0 CenterY=100 CenterZ=0 NormalX=0 NormalY=0 NormalZ=1 Radius=2
    g1: ArcOfCircle CenterX=0 CenterY=100 CenterZ=0 NormalX=0 NormalY=0 NormalZ=1 Radius=10 StartAngle=0.304689 EndAngle=2.8369
    g2: ArcOfCircle CenterX=0 CenterY=0 CenterZ=0 NormalX=0 NormalY=0 NormalZ=1 Radius=40 StartAngle=0.304693 EndAngle=2.8369
    g3: LineSegment StartX=-9.5394 StartY=103 StartZ=0 EndX=-38.1576 EndY=12 EndZ=0
    g4: LineSegment StartX=9.5394 StartY=103 StartZ=0 EndX=38.1576 EndY=12 EndZ=0
  constraints (15):
    c: PointOnObject(g0,g-2)
    c: Coincident(g1,g0)
    c: Coincident(g3,g1)
    c: Coincident(g3,g2)
    c: Coincident(g4,g1)
    c: Coincident(g4,g2)
    c: Equal(g2,g-3)
    c: Coincident(g2,g-1)
    c: Tangent(g-3,g3)
    c: Tangent(g4,g-3)
    c: Tangent(g1,g3)
    c: Tangent(g1,g4)
    c: DistanceY(g0) = 100
    c: Radius(g0) = 2
    c: Radius(g1) = 10
FEATURE [PartDesign::Pad] Pad009
  BaseFeature = -> Pocket013
  Length = 10
  Length2 = 100
  Placement = pos=(0,0,-127.292) rot=(0,0,1;0rad)
  Profile = -> Sketch029
  Reversed = true
  Type = 0
FEATURE [PartDesign::Body] Body006  label="Trigger"
  Group = -> [DatumPlane007,Sketch022,Pad006,DatumPlane008,DatumPlane009,Sketch023,Pocket010,Chamfer,Sketch024,Pocket011,PolarPattern,Fillet001,Sketch027,Pad008,Sketch028,Pocket013,Sketch029,Pad009]
  Origin = -> Body006Origin
  Tip = -> Pad009
FEATURE [App::Part] Part003  label="releasmechanism2"
  Group = -> [Body004,Body005,Body006]
  License = CC BY 3.0
  LicenseURL = http://creativecommons.org/licenses/by/3.0/
  Origin = -> Part003Origin
FEATURE [Mesh::Feature] Mesh002  label="Trigger (Meshed)"
